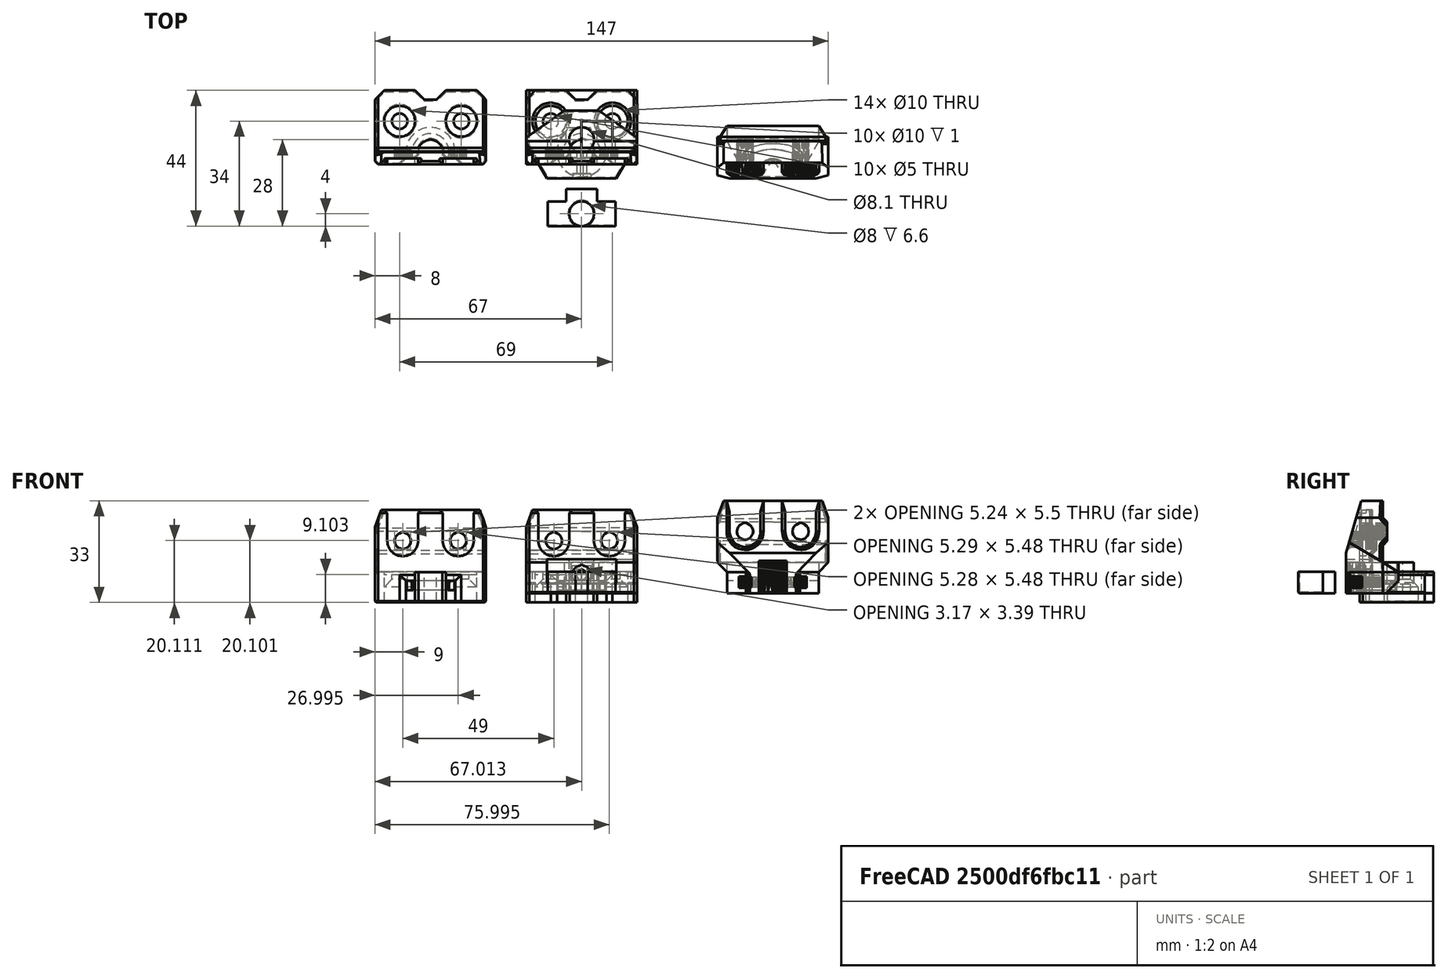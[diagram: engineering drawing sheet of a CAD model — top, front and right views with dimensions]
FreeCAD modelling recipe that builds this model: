
FCSTD DOCUMENT  (FreeCAD 0.18R14555 (Git shallow))
Label: bear-y-rod-mounter-lower-slim
License: All rights reserved
LicenseURL: http://en.wikipedia.org/wiki/All_rights_reserved
objects: Part::Cut×33, Part::Box×23, Part::Cylinder×22, Part::Feature×21, Part::Chamfer×17, Part::MultiFuse×16, Mesh::Feature×2, Part::Cone×2, Part::MultiCommon×1
note: 135 computed .brp shape members not serialized (recipe doc carries the construction recipe); baked Part::Feature solids carry a one-line shape summary decoded from their .brp

FEATURE [Mesh::Feature] Magnificent_Jaagub_1_  label="Magnificent Jaagub(1)"
FEATURE [Part::Feature] Magnificent_Jaagub_1_001
  shape: bbox 36 x 17 x 30 mm, 1432 faces, 0 solids (baked)
FEATURE [Part::Feature] Magnificent_Jaagub_1_001_solid  label="Magnificent_Jaagub_1_001 (Solid)"
  Placement = pos=(62,0,0) rot=(0,0,1;0rad)
  shape: bbox 36 x 17 x 30 mm, 1432 faces (baked)
FEATURE [Part::Box] Box  label="Cube"
  AttacherType = Attacher::AttachEngine3D
  Height = 10
  Length = 40
  Placement = pos=(-19,-13,0) rot=(0,0,1;0rad)
  Width = 28
FEATURE [Part::Feature] Magnificent_Jaagub_1_001_solid001  label="base"
  shape: bbox 36 x 17 x 30 mm, 1432 faces (baked)
FEATURE [Part::Cut] Cut
  Base = -> Magnificent_Jaagub_1_001_solid001
  Placement = pos=(0,-3.5,0) rot=(0,0,1;0rad)
  Tool = -> Box
FEATURE [Part::Box] Box001  label="Cube001"
  AttacherType = Attacher::AttachEngine3D
  Height = 11
  Length = 36
  Placement = pos=(-18,-8.5,0) rot=(0,0,1;0rad)
  Width = 22
FEATURE [Part::Feature] Body001
  shape: bbox 7.75 x 13.25 x 10 mm, 5 faces (baked)
FEATURE [Part::Feature] Body002
  Placement = pos=(-1e-15,0,10) rot=(0,1,0;3.14159rad)
  shape: bbox 7.75 x 13.25 x 10 mm, 5 faces (baked)
FEATURE [Part::Feature] Body003
  Placement = pos=(0,0,1) rot=(0,0,1;0rad)
  shape: bbox 7.75 x 13.25 x 10 mm, 5 faces (baked)
FEATURE [Part::MultiFuse] Fusion
  Shapes = -> [Body003,Body001]
FEATURE [Part::Feature] Body004
  Placement = pos=(-1e-15,0,11) rot=(0,1,0;3.14159rad)
  shape: bbox 7.75 x 13.25 x 10 mm, 5 faces (baked)
FEATURE [Part::MultiFuse] Fusion001
  Shapes = -> [Body004,Body002]
FEATURE [Part::Box] Box002  label="Cube002"
  AttacherType = Attacher::AttachEngine3D
  Height = 1
  Length = 36
  Placement = pos=(-18,3.5,10) rot=(0,0,1;0rad)
  Width = 14
FEATURE [Part::Cut] Cut001
  Base = -> Box001
  Tool = -> Fusion
FEATURE [Part::Cut] Cut002
  Base = -> Cut001
  Tool = -> Fusion001
FEATURE [Part::Cut] Cut003
  Base = -> Cut002
  Tool = -> Box002
FEATURE [Part::Cylinder] Cylinder001
  Angle = 360
  AttacherType = Attacher::AttachEngine3D
  Height = 11
  Placement = pos=(0,4,0) rot=(0,0,1;0rad)
  Radius = 4.05
FEATURE [Part::Cut] Cut004
  Base = -> Cut003
  Tool = -> Cylinder001
FEATURE [Part::Feature] Body005
  shape: bbox 14 x 10 x 10 mm, 5 faces (baked)
FEATURE [Part::Feature] Body006
  Placement = pos=(-1e-15,0,10) rot=(0,1,0;3.14159rad)
  shape: bbox 14 x 10 x 10 mm, 5 faces (baked)
FEATURE [Part::Cut] Cut005
  Base = -> Cut004
  Tool = -> Body006
FEATURE [Part::Cut] Cut006
  Base = -> Cut005
  Tool = -> Body005
FEATURE [Part::Chamfer] Chamfer
  Base = -> Cut006
  Edges = 2 edges r=0.4: [Edge5,Edge44]
FEATURE [Part::Box] Box003  label="Cube003"
  AttacherType = Attacher::AttachEngine3D
  Height = 3
  Length = 40
  Placement = pos=(-20,-10,0) rot=(0,0,1;0rad)
  Width = 24
FEATURE [Part::Cut] Cut008
  Base = -> Chamfer
  Tool = -> Box003
FEATURE [Part::Box] Box004  label="Cube004"
  AttacherType = Attacher::AttachEngine3D
  Height = 7
  Length = 6
  Placement = pos=(-3,-4,2) rot=(0,0,1;0rad)
  Width = 2
FEATURE [Part::Cylinder] Cylinder002
  Angle = 360
  AttacherType = Attacher::AttachEngine3D
  Height = 15
  Placement = pos=(0,2,6) rot=(1,0,0;1.5708rad)
  Radius = 1.6
FEATURE [Part::Cylinder] Cylinder003
  Angle = 360
  AttacherType = Attacher::AttachEngine3D
  Height = 3
  Placement = pos=(0,-7,6) rot=(1,0,0;1.5708rad)
  Radius = 3
FEATURE [Part::Cylinder] Cylinder004
  Angle = 360
  AttacherType = Attacher::AttachEngine3D
  Height = 15
  Placement = pos=(0,2,7.3) rot=(1,0,0;1.5708rad)
  Radius = 0.5
FEATURE [Part::Cylinder] Cylinder005
  Angle = 360
  AttacherType = Attacher::AttachEngine3D
  Height = 3
  Placement = pos=(0,-7,8.8) rot=(1,0,0;1.5708rad)
  Radius = 0.5
FEATURE [Part::Cut] Cut009
  Base = -> Cut008
  Tool = -> Box004
FEATURE [Part::MultiFuse] Fusion002
  Shapes = -> [Cylinder002,Cylinder003,Cylinder004,Cylinder005]
FEATURE [Part::Chamfer] Chamfer001
  Base = -> Cut009
  Edges = 8 edges r=0.4: [Edge5,Edge23,Edge24,Edge25,Edge26,Edge27,Edge28,Edge29]
FEATURE [Part::Cut] Cut010
  Base = -> Chamfer001
  Tool = -> Fusion002
FEATURE [Part::Box] Box005  label="Cube005"
  AttacherType = Attacher::AttachEngine3D
  Height = 1
  Length = 12
  Placement = pos=(-6,-4,6.8) rot=(0,0,1;0rad)
  Width = 4
FEATURE [Part::Chamfer] Chamfer002
  Base = -> Cut010
  Edges = 5 edges r=0.2: [Edge50,Edge51,Edge52,Edge53,Edge54]
FEATURE [Part::Box] Box006  label="Cube006"
  AttacherType = Attacher::AttachEngine3D
  Height = 10
  Length = 10
  Width = 10
FEATURE [Part::Box] Box007  label="Cube007"
  AttacherType = Attacher::AttachEngine3D
  Height = 32
  Length = 40
  Placement = pos=(-20,-14,0) rot=(0,0,1;0rad)
  Width = 10
FEATURE [Part::Cut] Cut011
  Base = -> Cut
  Placement = pos=(0,0,-3) rot=(0,0,1;0rad)
  Tool = -> Box007
FEATURE [Part::Cylinder] Cylinder
  Angle = 360
  AttacherType = Attacher::AttachEngine3D
  Height = 2
  Placement = pos=(-9,-3,17) rot=(1,0,0;1.5708rad)
  Radius = 5
FEATURE [Part::Cylinder] Cylinder006
  Angle = 360
  AttacherType = Attacher::AttachEngine3D
  Height = 2
  Placement = pos=(-9,-3,21.8) rot=(1,0,0;1.5708rad)
  Radius = 0.5
FEATURE [Part::Box] Box008  label="Cube008"
  AttacherType = Attacher::AttachEngine3D
  Height = 7
  Length = 36
  Placement = pos=(-18,-4,0) rot=(0,0,1;0rad)
  Width = 24
FEATURE [Part::Cylinder] Cylinder007
  Angle = 360
  AttacherType = Attacher::AttachEngine3D
  Height = 7
  Radius = 4
FEATURE [Part::Box] Box009  label="Cube009"
  AttacherType = Attacher::AttachEngine3D
  Height = 10
  Length = 36
  Placement = pos=(-18,-4,0) rot=(0,0,1;0rad)
  Width = 4
FEATURE [Part::Cylinder] Cylinder009
  Angle = 360
  AttacherType = Attacher::AttachEngine3D
  Height = 1
  Placement = pos=(10,10,6) rot=(0,0,1;0rad)
  Radius = 5
FEATURE [Part::Cylinder] Cylinder010
  Angle = 360
  AttacherType = Attacher::AttachEngine3D
  Height = 1
  Placement = pos=(-10,10,6) rot=(0,0,1;0rad)
  Radius = 5
FEATURE [Part::Cylinder] Cylinder011
  Angle = 360
  AttacherType = Attacher::AttachEngine3D
  Height = 10
  Placement = pos=(10,10,0) rot=(0,0,1;0rad)
  Radius = 2.5
FEATURE [Part::Cylinder] Cylinder012
  Angle = 360
  AttacherType = Attacher::AttachEngine3D
  Height = 10
  Placement = pos=(-10,10,0) rot=(0,0,1;0rad)
  Radius = 2.5
FEATURE [Part::Chamfer] Chamfer003
  Base = -> Box009
  Edges = 2 edges r=0.5: [Edge3,Edge7]
FEATURE [Part::MultiFuse] Fusion003003  label="top-screw-slot"
  Placement = pos=(0,1,0) rot=(0,0,1;0rad)
  Shapes = -> [Cylinder,Cylinder006]
FEATURE [Part::Feature] Fusion003003001  label="top-screw-slot001"
  Placement = pos=(18,1,0) rot=(0,0,1;0rad)
  shape: bbox 10 x 2 x 10.3 mm, 9 faces (baked)
FEATURE [Part::Cut] Cut012
  Base = -> Cut011
  Tool = -> Fusion003003
FEATURE [Part::Cut] Cut013
  Base = -> Cut012
  Tool = -> Fusion003003001
FEATURE [Part::MultiFuse] Fusion003003002
  Shapes = -> [Cylinder011,Cylinder009]
FEATURE [Part::MultiFuse] Fusion003003003
  Shapes = -> [Cylinder010,Cylinder012]
FEATURE [Part::Chamfer] Chamfer004
  Base = -> Box008
  Edges = 2 edges r=1: [Edge2,Edge6]
FEATURE [Part::MultiFuse] Fusion003003004
  Shapes = -> [Chamfer004,Chamfer003]
FEATURE [Part::Cut] Cut014
  Base = -> Fusion003003004
  Tool = -> Fusion003003002
FEATURE [Part::Cut] Cut015
  Base = -> Cut014
  Tool = -> Fusion003003003
FEATURE [Part::Cylinder] Cylinder008
  Angle = 360
  AttacherType = Attacher::AttachEngine3D
  Height = 7
  Radius = 8
FEATURE [Part::Cut] Cut016
  Base = -> Cut015
  Tool = -> Cylinder007
FEATURE [Part::Box] Box010  label="Cube010"
  AttacherType = Attacher::AttachEngine3D
  Height = 10
  Length = 7
  Placement = pos=(-3.5,-10,0) rot=(0,0,1;0rad)
  Width = 10
FEATURE [Part::Cut] Cut017
  Base = -> Cut016
  Tool = -> Box010
FEATURE [Part::Feature] Cut017001  label="Cut018"
  shape: bbox 36 x 24 x 10 mm, 26 faces (baked)
FEATURE [Part::Box] Box011  label="Cube011"
  AttacherType = Attacher::AttachEngine3D
  Height = 6
  Length = 20
  Placement = pos=(-10,-9,0) rot=(0,0,1;0rad)
  Width = 3
FEATURE [Part::Box] Box012  label="chmp1"
  AttacherType = Attacher::AttachEngine3D
  Height = 30
  Length = 2
  Placement = pos=(-18,-4,0) rot=(0,0,1;0rad)
  Width = 2
FEATURE [Part::Box] Box013  label="chmp2"
  AttacherType = Attacher::AttachEngine3D
  Height = 30
  Length = 2
  Placement = pos=(16,-4,0) rot=(0,0,1;0rad)
  Width = 2
FEATURE [Part::Chamfer] Chamfer006
  Base = -> Box012
  Edges = 1 edges r=1: [Edge7]
  Placement = pos=(-1,-1,0) rot=(0,0,1;0rad)
FEATURE [Part::Chamfer] Chamfer007
  Base = -> Box013
  Edges = 1 edges r=1: [Edge3]
  Placement = pos=(1,-1,0) rot=(0,0,1;0rad)
FEATURE [Part::Feature] Chamfer007001  label="Chamfer008"
  Placement = pos=(1,-1,0) rot=(0,0,1;0rad)
  shape: bbox 2 x 2 x 30 mm, 7 faces (baked)
FEATURE [Part::Feature] Chamfer006001  label="Chamfer009"
  Placement = pos=(-1,-1,0) rot=(0,0,1;0rad)
  shape: bbox 2 x 2 x 30 mm, 7 faces (baked)
FEATURE [Part::Cut] Cut017002
  Base = -> Cut017001
  Tool = -> Chamfer006
FEATURE [Part::Cut] Cut017003
  Base = -> Cut013
  Tool = -> Chamfer006001
FEATURE [Part::Cut] Cut017004
  Base = -> Cut017003
  Tool = -> Chamfer007
FEATURE [Part::Cut] Cut017005
  Base = -> Cut017002
  Tool = -> Chamfer007001
FEATURE [Part::Chamfer] Chamfer007002
  Base = -> Cut017005
  Edges = 2 edges r=3: [Edge18,Edge26]
FEATURE [Part::Box] Box014  label="Cube012"
  AttacherType = Attacher::AttachEngine3D
  Height = 10
  Length = 10
  Placement = pos=(-5,24,0) rot=(0,0,1;0rad)
  Width = 10
FEATURE [Part::Chamfer] Chamfer007003
  Base = -> Box014
  Edges = 2 edges r=3: [Edge1,Edge5]
  Placement = pos=(0,-7,0) rot=(0,0,1;0rad)
FEATURE [Part::Cut] Cut017006
  Base = -> Chamfer007002
  Tool = -> Chamfer007003
FEATURE [Part::Box] Box015  label="Cube013"
  AttacherType = Attacher::AttachEngine3D
  Height = 10
  Length = 10
  Placement = pos=(-4,-6,0) rot=(0,0,1;0rad)
  Width = 6
FEATURE [Part::Chamfer] Chamfer007004
  Base = -> Box015
  Edges = 2 edges r=2: [Edge3,Edge7]
  Placement = pos=(-1,0,0) rot=(0,0,1;0rad)
FEATURE [Part::Cut] Cut017007
  Base = -> Cut017006
  Tool = -> Chamfer007004
FEATURE [Part::Chamfer] Chamfer007005
  Base = -> Box011
  Edges = 3 edges r=2: [Edge3,Edge7,Edge12]
  Placement = pos=(0,4,0) rot=(0,0,1;0rad)
FEATURE [Part::Cut] Cut017008
  Base = -> Cut017007
  Tool = -> Chamfer007005
FEATURE [Part::Cylinder] Cylinder013
  Angle = 360
  AttacherType = Attacher::AttachEngine3D
  Height = 3
  Radius = 6
FEATURE [Part::Cylinder] Cylinder014
  Angle = 360
  AttacherType = Attacher::AttachEngine3D
  Height = 3
  Radius = 8
FEATURE [Part::Box] Box016  label="Cube014"
  AttacherType = Attacher::AttachEngine3D
  Height = 3
  Length = 36
  Placement = pos=(-18,-4,30) rot=(0,0,1;0rad)
  Width = 3
FEATURE [Part::Chamfer] Chamfer007010
  Base = -> Box016
  Edges = 1 edges r=1: [Edge11]
  Placement = pos=(0,-2,-4) rot=(0,0,1;0rad)
FEATURE [Part::Cut] Cut017009
  Base = -> Cylinder014
  Placement = pos=(0,0,1) rot=(0,0,1;0rad)
  Tool = -> Cylinder013
FEATURE [Part::Cylinder] Cylinder015
  Angle = 360
  AttacherType = Attacher::AttachEngine3D
  Height = 7
  Placement = pos=(-10,10,0) rot=(0,0,1;0rad)
  Radius = 6
FEATURE [Part::Cylinder] Cylinder016
  Angle = 360
  AttacherType = Attacher::AttachEngine3D
  Height = 7
  Placement = pos=(10,10,0) rot=(0,0,1;0rad)
  Radius = 6
FEATURE [Part::Cylinder] Cylinder019
  Angle = 360
  AttacherType = Attacher::AttachEngine3D
  Height = 7
  Placement = pos=(-10,10,0) rot=(0,0,1;0rad)
  Radius = 2.5
FEATURE [Part::Cylinder] Cylinder020
  Angle = 360
  AttacherType = Attacher::AttachEngine3D
  Height = 7
  Placement = pos=(10,10,0) rot=(0,0,1;0rad)
  Radius = 2.5
FEATURE [Mesh::Feature] y_bearing_holder
  Placement = pos=(0,-1,0) rot=(0,0,1;0rad)
FEATURE [Part::Cone] Cone
  Angle = 360
  AttacherType = Attacher::AttachEngine3D
  Height = 2.5
  Placement = pos=(10,10,2) rot=(0,0,1;0rad)
  Radius1 = 5
  Radius2 = 2.5
FEATURE [Part::Cylinder] Cylinder021
  Angle = 360
  AttacherType = Attacher::AttachEngine3D
  Height = 2
  Placement = pos=(10,10,0) rot=(0,0,1;0rad)
  Radius = 5
FEATURE [Part::Cylinder] Cylinder022
  Angle = 360
  AttacherType = Attacher::AttachEngine3D
  Height = 2
  Placement = pos=(-10,10,0) rot=(0,0,1;0rad)
  Radius = 5
FEATURE [Part::Cone] Cone001
  Angle = 360
  AttacherType = Attacher::AttachEngine3D
  Height = 2.5
  Placement = pos=(-10,10,2) rot=(0,0,1;0rad)
  Radius1 = 5
  Radius2 = 2.5
FEATURE [Part::MultiFuse] Fusion003003006002
  Shapes = -> [Cylinder019,Cylinder020]
FEATURE [Part::MultiFuse] Fusion003003006003
  Shapes = -> [Cylinder021,Cylinder022]
FEATURE [Part::MultiFuse] Fusion003003006004
  Shapes = -> [Cone001,Cone]
FEATURE [Part::Box] Box017  label="Cube015"
  AttacherType = Attacher::AttachEngine3D
  Height = 10
  Length = 10
  Placement = pos=(-14,-4,17) rot=(0,0,1;0rad)
  Width = 2
FEATURE [Part::Box] Box018  label="Cube016"
  AttacherType = Attacher::AttachEngine3D
  Height = 2
  Length = 12
  Placement = pos=(-15,-4,28) rot=(0,0,1;0rad)
  Width = 2
FEATURE [Part::Chamfer] Chamfer007014
  Base = -> Box018
  Edges = 2 edges r=1: [Edge4,Edge8]
  Placement = pos=(0,0,-2) rot=(0,0,1;0rad)
FEATURE [Part::MultiFuse] Fusion003003006005
  Shapes = -> [Box017,Chamfer007014]
FEATURE [Part::Feature] Fusion003003006005001  label="Fusion003003006006"
  Placement = pos=(18,0,0) rot=(0,0,1;0rad)
  shape: bbox 12 x 2 x 11 mm, 14 faces (baked)
FEATURE [Part::Cylinder] Cylinder023
  Angle = 360
  AttacherType = Attacher::AttachEngine3D
  Height = 10
  Radius = 4
FEATURE [Part::Box] Box019  label="Cube017"
  AttacherType = Attacher::AttachEngine3D
  Height = 7
  Length = 10
  Placement = pos=(-5,-4,0) rot=(0,0,1;0rad)
  Width = 12
FEATURE [Part::Box] Box020  label="Cube018"
  AttacherType = Attacher::AttachEngine3D
  Height = 7
  Length = 22
  Placement = pos=(-11,-4,0) rot=(0,0,1;0rad)
  Width = 8
FEATURE [Part::MultiFuse] Fusion003003006005002
  Shapes = -> [Box019,Box020]
FEATURE [Part::Box] Box021  label="Cube019"
  AttacherType = Attacher::AttachEngine3D
  Height = 6.8
  Length = 4
  Placement = pos=(-2,-8,0) rot=(0,0,1;0rad)
  Width = 10
FEATURE [Part::Chamfer] Chamfer007017
  Base = -> Fusion003003006005002
  Edges = 3 edges r=0.4: [Edge14,Edge20,Edge33]
FEATURE [Part::Cut] Cut017016002
  Base = -> Chamfer007017
  Tool = -> Cylinder023
FEATURE [Part::Cut] Cut017016003
  Base = -> Cut017016002
  Tool = -> Box021
FEATURE [Part::Feature] Cut017016003001  label="Cut017016004"
  shape: bbox 22 x 12 x 7 mm, 17 faces (baked)
FEATURE [Part::Chamfer] Chamfer007018
  Base = -> Cut017016003001
  Edges = 3 edges r=0.4: [Edge48,Edge49,Edge50]
  Placement = pos=(0,-20,0) rot=(0,0,1;0rad)
FEATURE [Part::Cut] Cut017016003002
  Base = -> Cut017008
  Tool = -> Cut017009
FEATURE [Part::Cut] Cut017016003003
  Base = -> Cut017004
  Tool = -> Fusion003003006005
FEATURE [Part::Cut] Cut017016003004
  Base = -> Cut017016003003
  Tool = -> Fusion003003006005001
FEATURE [Part::Cut] Cut017016003005
  Base = -> Cut017016003004
  Tool = -> Chamfer007010
FEATURE [Part::Cut] Cut017016003006
  Base = -> Cut017016003002
  Tool = -> Fusion003003006003
FEATURE [Part::Cut] Cut017016003007
  Base = -> Cut017016003006
  Tool = -> Fusion003003006004
FEATURE [Part::MultiFuse] Fusion003003006005003
  Shapes = -> [Cut017016003007,Cut017016003005]
FEATURE [Part::MultiFuse] Fusion003003006005004  label="7mm"
  Shapes = -> [Box005,Fusion003003006005003]
FEATURE [Part::Feature] Fusion003003006005004001  label="Fusion003003006005005"
  shape: bbox 36 x 24 x 27 mm, 534 faces (baked)
FEATURE [Part::Box] Box022  label="Cube020"
  AttacherType = Attacher::AttachEngine3D
  Height = 1
  Length = 38
  Placement = pos=(-19,-9,0) rot=(0,0,1;0rad)
  Width = 32
FEATURE [Part::MultiCommon] Common
  Shapes = -> [Fusion003003006005004001,Box022]
FEATURE [Part::Feature] Common001
  Placement = pos=(0,0,1) rot=(0,0,1;0rad)
  shape: bbox 36 x 24 x 1 mm, 26 faces (baked)
FEATURE [Part::Feature] Common002
  Placement = pos=(0,0,-1) rot=(0,0,1;0rad)
  shape: bbox 36 x 24 x 1 mm, 26 faces (baked)
FEATURE [Part::MultiFuse] Fusion003003006005004002
  Placement = pos=(0,0,-2) rot=(0,0,1;0rad)
  Shapes = -> [Common002,Common,Common001]
FEATURE [Part::Feature] Fusion003003006005004003
  shape: bbox 36 x 24 x 27 mm, 534 faces (baked)
FEATURE [Part::MultiFuse] Fusion003003006005004004  label="10mm"
  Shapes = -> [Fusion003003006005004003,Fusion003003006005004002]
FEATURE [Part::Feature] Fusion003003006005004005  label="7mm001"
  shape: bbox 36 x 24 x 27 mm, 349 faces (baked)
FEATURE [Part::Feature] Fusion003003006005004004001  label="10mm001"
  Placement = pos=(-49,0,0) rot=(0,0,1;0rad)
  shape: bbox 36 x 24 x 30 mm, 349 faces (baked)
FEATURE [Part::Chamfer] Chamfer007019
  Base = -> Fusion003003006005004004001
  Edges = 24 edges r=0.4: [Edge1,Edge2,Edge3,Edge4,Edge5,Edge6,Edge7,Edge8,Edge9,Edge10,Edge11,Edge12,Edge13,Edge14,Edge15,Edge16,Edge17,Edge18,Edge19,Edge20,Edge21,Edge22,Edge23,Edge24]
FEATURE [Part::Chamfer] Chamfer007020
  Base = -> Fusion003003006005004005
  Edges = 23 edges r=0.4: [Edge1,Edge2,Edge3,Edge4,Edge5,Edge6,Edge7,Edge8,Edge9,Edge10,Edge11,Edge12,Edge13,Edge14,Edge15,Edge16,Edge17,Edge19,Edge20,Edge21,Edge22,Edge23,Edge24]
